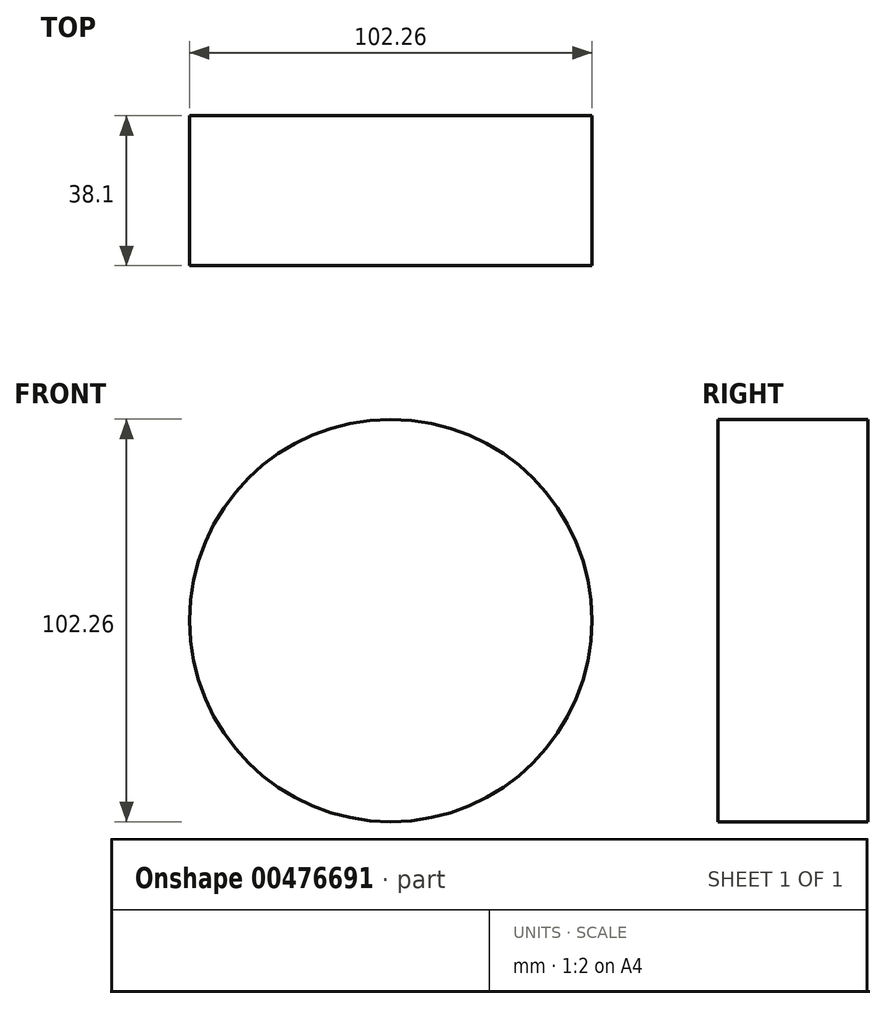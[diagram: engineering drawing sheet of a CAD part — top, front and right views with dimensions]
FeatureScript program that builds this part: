
annotation { "Feature Type Name" : "Feature", "Feature Type Description" : "" }
export const myFeature = defineFeature(function(context is Context, id is Id, definition is map)
    precondition{}
    {
        {
            var Q0;
            Q0=qCreatedBy(makeId("Front.planeOp"),FACE);
            var sketch = newSketch(context, id + "F0", { "sketchPlane" : qUnion([Q0])});
            skCircle(sketch, "E0", {"center": v(0, 0) * mm, "radius": 51.13 * mm});
            skSolve(sketch);
        }
        {
            var Q0;
            Q0=makeQuery(id+"F0.imprint","IMPRINT",FACE,{"disambiguationData":[TD([[makeQuery(id+"F0.imprint","IMPRINT",EDGE,{"derivedFrom":sQuery(id+"F0.wireOp",EDGE,"E0")}),1.0]])]});
            extrude(context, id + "F1", {"entities" : qUnion([Q0]), "depth" : 38.1 * mm});
        }
    });
